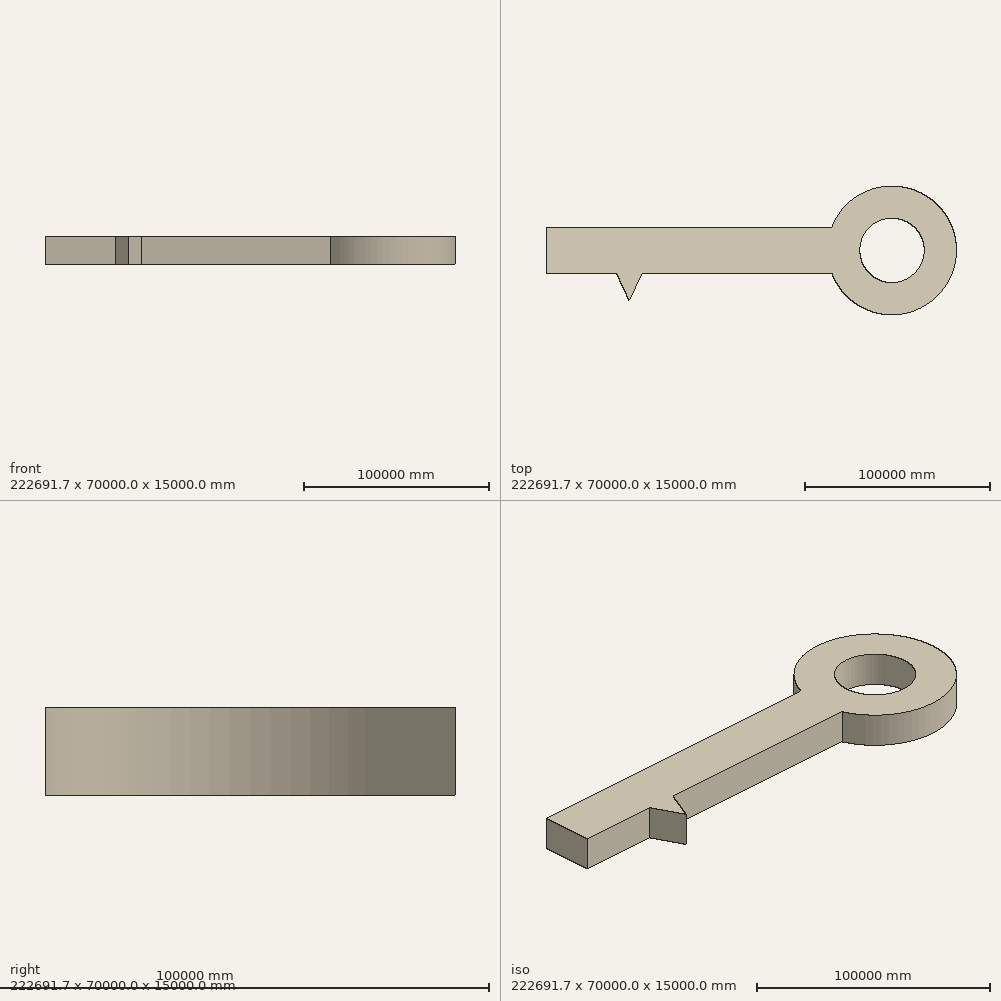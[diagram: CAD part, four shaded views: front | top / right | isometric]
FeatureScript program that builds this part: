
annotation { "Feature Type Name" : "Feature", "Feature Type Description" : "" }
export const myFeature = defineFeature(function(context is Context, id is Id, definition is map)
    precondition{}
    {
        {
            var Q0;
            Q0=qCreatedBy(makeId("Top.planeOp"),FACE);
            var sketch = newSketch(context, id + "F0", { "sketchPlane" : qUnion([Q0])});
            skLineSegment(sketch, "E0.bottom", {"start": v(0, 40000.06) * mm, "end": v(-155000, 40000.06) * mm});
            skLineSegment(sketch, "E0.top", {"start": v(0, 15000.06) * mm, "end": v(-155000, 15000.06) * mm});
            skLineSegment(sketch, "E0.left", {"start": v(0, 40000.06) * mm, "end": v(0, 15000.06) * mm});
            skLineSegment(sketch, "E0.right", {"start": v(-155000, 40000.06) * mm, "end": v(-155000, 15000.06) * mm});
            skLineSegment(sketch, "E1.bottom", {"start": v(-155000, 15000.06) * mm, "end": v(-145000, 15000.06) * mm});
            skLineSegment(sketch, "E1.top", {"start": v(-155000, -14999.94) * mm, "end": v(-145000, -14999.94) * mm});
            skLineSegment(sketch, "E1.left", {"start": v(-155000, 15000.06) * mm, "end": v(-155000, -14999.94) * mm});
            skLineSegment(sketch, "E1.right", {"start": v(-145000, 15000.06) * mm, "end": v(-145000, -14999.94) * mm});
            skLineSegment(sketch, "E2.bottom", {"start": v(-135000, 15000.06) * mm, "end": v(-127000, 15000.06) * mm});
            skLineSegment(sketch, "E2.top", {"start": v(-135000, 0.06) * mm, "end": v(-127000, 0.06) * mm});
            skLineSegment(sketch, "E2.left", {"start": v(-135000, 15000.06) * mm, "end": v(-135000, 0.06) * mm});
            skLineSegment(sketch, "E2.right", {"start": v(-127000, 15000.06) * mm, "end": v(-127000, 0.06) * mm});
            skLineSegment(sketch, "E3", {"start": v(-117000, 15000.06) * mm, "end": v(-110000, 0) * mm});
            skLineSegment(sketch, "E4", {"start": v(-103000, 15000.06) * mm, "end": v(-110000, 0) * mm});
            skArc(sketch, "E5", {"start": v(0, 15000.06) * mm, "mid": v(67691.74, 27500.06) * mm, "end": v(0, 40000.06) * mm});
            skCircle(sketch, "E6", {"center": v(32691.74, 27500.06) * mm, "radius": 17500 * mm});
            skSolve(sketch);
        }
        {
            var Q0;
            Q0=makeQuery(id+"F0.imprint","IMPRINT",FACE,{"disambiguationData":[TD([[makeQuery(id+"F0.imprint","IMPRINT",EDGE,{"derivedFrom":sQuery(id+"F0.wireOp",EDGE,"E0.bottom")}),1.0]])]});
            var Q1;
            Q1=makeQuery(id+"F0.imprint","IMPRINT",FACE,{"disambiguationData":[TD([[makeQuery(id+"F0.imprint","IMPRINT",EDGE,{"derivedFrom":sQuery(id+"F0.wireOp",EDGE,"E2.bottom")}),-1.0]])]});
            var Q2;
            {var subQ1=sQuery(id+"F0.wireOp",EDGE,"E3");Q2=makeQuery(id+"F0.imprint","IMPRINT",FACE,{"disambiguationData":[TD([[makeQuery(id+"F0.imprint","IMPRINT",EDGE,{"derivedFrom":subQ1}),1.0]])]});}
            var Q3;
            Q3=makeQuery(id+"F0.imprint","IMPRINT",FACE,{"disambiguationData":[TD([[makeQuery(id+"F0.imprint","IMPRINT",EDGE,{"derivedFrom":sQuery(id+"F0.wireOp",EDGE,"E0.left")}),1.0]])]});
            var Q4;
            Q4=makeQuery(id+"F0.imprint","IMPRINT",FACE,{"disambiguationData":[TD([[makeQuery(id+"F0.imprint","IMPRINT",EDGE,{"derivedFrom":sQuery(id+"F0.wireOp",EDGE,"E1.bottom")}),-1.0]])]});
            extrude(context, id + "F1", {"entities" : qUnion([Q0, Q1, Q2, Q3, Q4]), "depth" : 15000 * mm});
        }
    });
